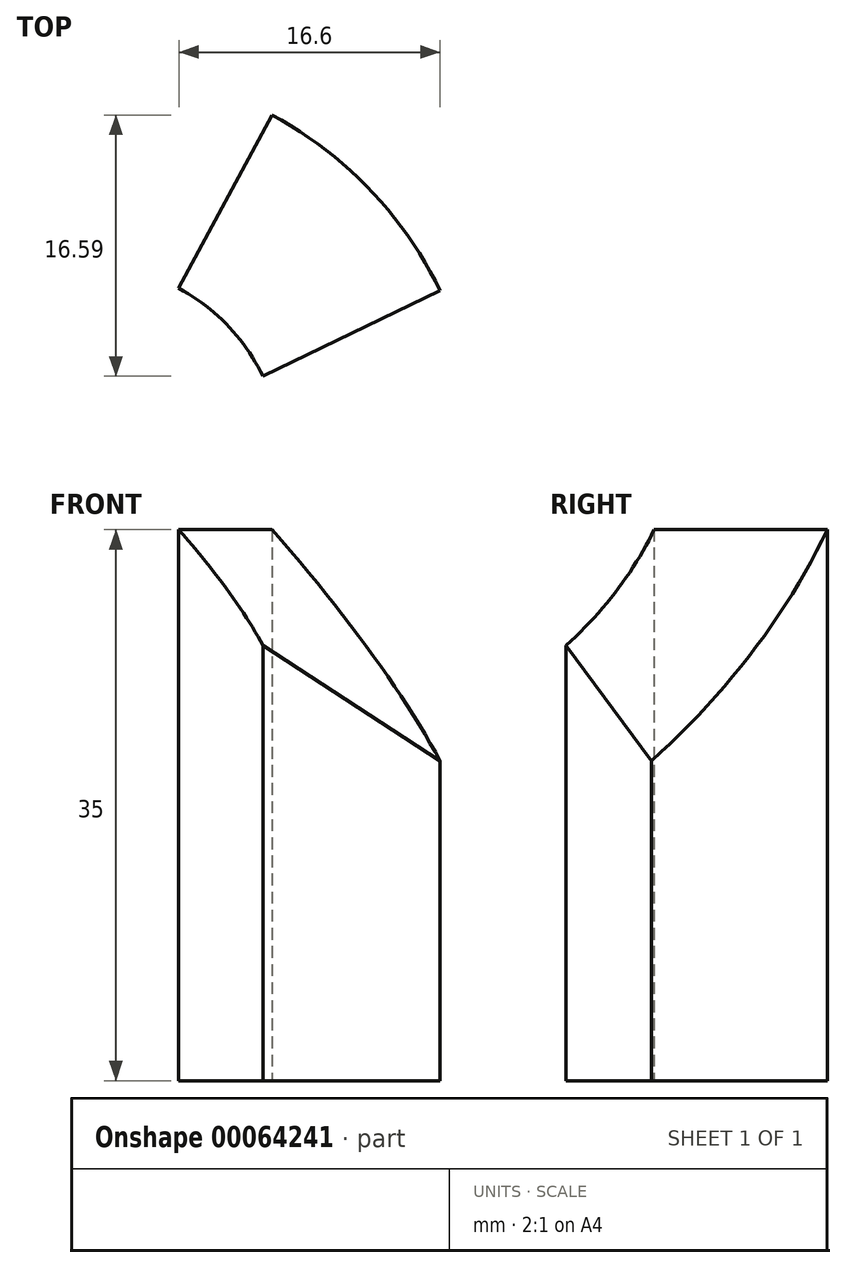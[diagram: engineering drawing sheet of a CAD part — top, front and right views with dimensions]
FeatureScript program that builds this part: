
annotation { "Feature Type Name" : "Feature", "Feature Type Description" : "" }
export const myFeature = defineFeature(function(context is Context, id is Id, definition is map)
    precondition{}
    {
        {
            var Q0;
            Q0=qCreatedBy(makeId("Top.planeOp"),FACE);
            var sketch = newSketch(context, id + "F0", { "sketchPlane" : qUnion([Q0])});
            skCircle(sketch, "E0", {"center": v(0, 0) * mm, "radius": 25 * mm, "construction": true});
            skLineSegment(sketch, "E1", {"start": v(5.93, 11) * mm, "end": v(11.85, 22.01) * mm});
            skLineSegment(sketch, "E2", {"start": v(11.26, 5.42) * mm, "end": v(22.53, 10.84) * mm});
            skArc(sketch, "E3", {"start": v(22.53, 10.84) * mm, "mid": v(18.07, 17.27) * mm, "end": v(11.85, 22.01) * mm});
            skArc(sketch, "E4", {"start": v(11.26, 5.42) * mm, "mid": v(9.04, 8.64) * mm, "end": v(5.93, 11) * mm});
            skSolve(sketch);
        }
        {
            var Q0;
            Q0 = qSketchRegion(id + "F0", true);
            extrude(context, id + "F1", {"entities" : qUnion([Q0]), "depth" : 35 * mm});
        }
        {
            var Q0;
            Q0=makeQuery(id+"F1.opExtrude","CAP_EDGE",EDGE,{"disambiguationData":[OSD([sQuery(id+"F0.wireOp",EDGE,"E1")])],"isStart":false});
            cPlane(context, id + "F2", {"entities" : qUnion([Q0]), "cplaneType" : CPlaneType.LINE_ANGLE, "offset" : 150 * mm, "angle" : 45 * degree, "width" : 150 * mm, "height" : 150 * mm});
        }
        {
            var Q0;
            Q0=qCreatedBy(id+"F2.planeOp",FACE);
            var sketch = newSketch(context, id + "F3", { "sketchPlane" : qUnion([Q0])});
            skLineSegment(sketch, "E5.bottom", {"start": v(-18.14, 36.63) * mm, "end": v(11.15, 36.63) * mm});
            skLineSegment(sketch, "E5.top", {"start": v(-18.14, 12.18) * mm, "end": v(11.15, 12.18) * mm});
            skLineSegment(sketch, "E5.left", {"start": v(-18.14, 36.63) * mm, "end": v(-18.14, 12.18) * mm});
            skLineSegment(sketch, "E5.right", {"start": v(11.15, 36.63) * mm, "end": v(11.15, 12.18) * mm});
            skSolve(sketch);
        }
        {
            var Q0;
            Q0 = qSketchRegion(id + "F3", true);
            extrude(context, id + "F4", {"entities" : qUnion([Q0]), "operationType" : NewBodyOperationType.REMOVE, "depth" : 25 * mm});
        }
    });
